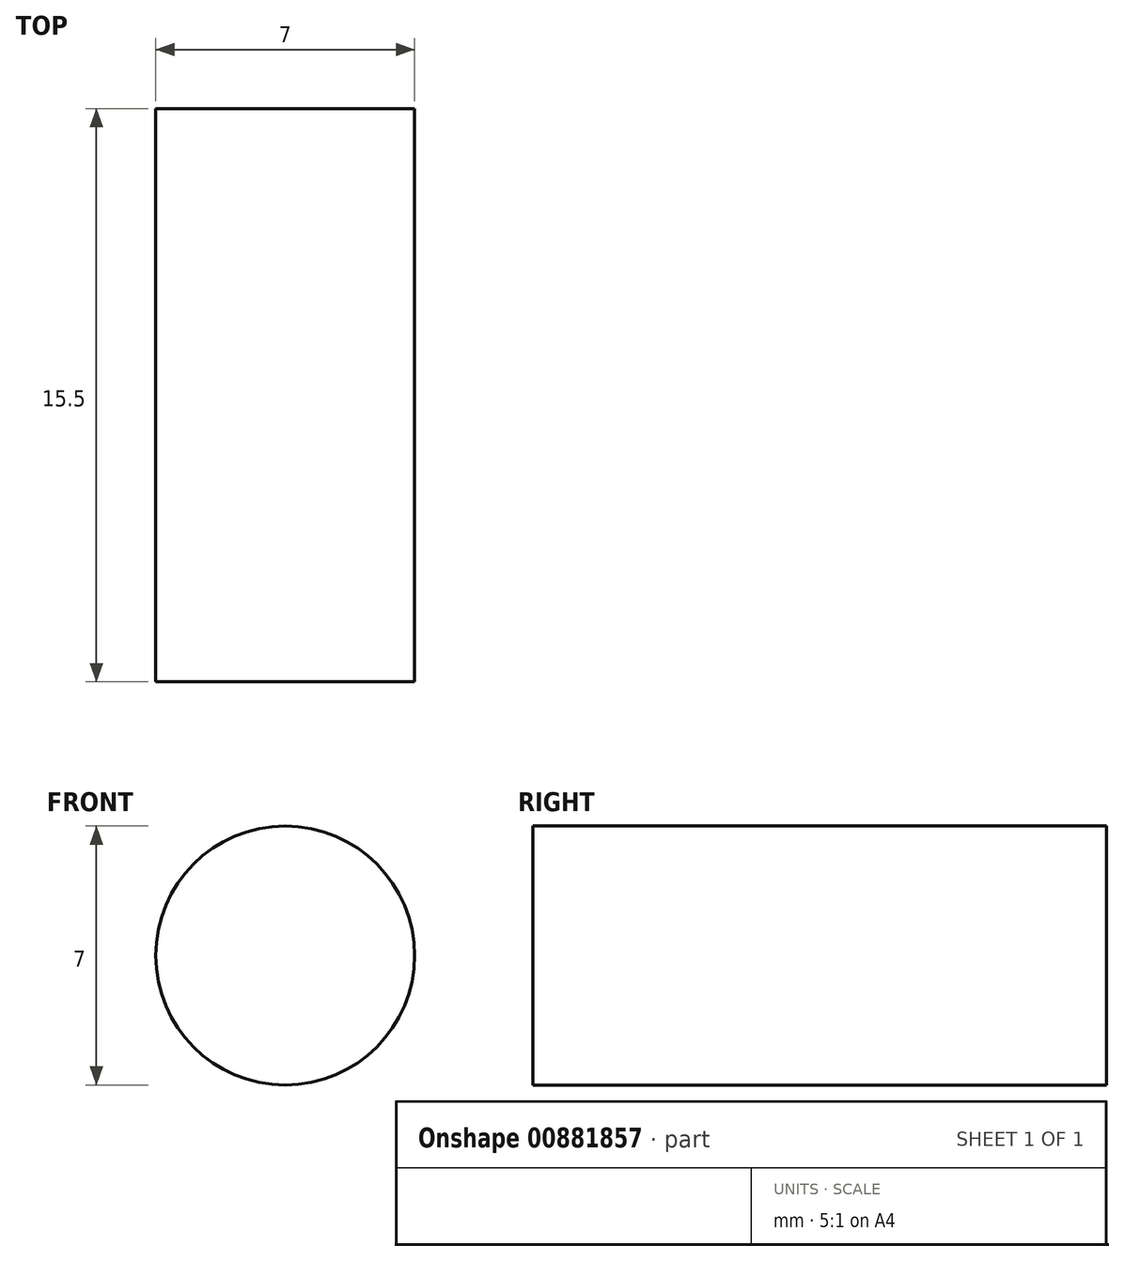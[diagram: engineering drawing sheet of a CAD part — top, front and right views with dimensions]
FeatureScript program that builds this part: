
annotation { "Feature Type Name" : "Feature", "Feature Type Description" : "" }
export const myFeature = defineFeature(function(context is Context, id is Id, definition is map)
    precondition{}
    {
        {
            var Q0;
            Q0=qCreatedBy(makeId("Top.planeOp"),FACE);
            var sketch = newSketch(context, id + "F0", { "sketchPlane" : qUnion([Q0])});
            skLineSegment(sketch, "E0.bottom", {"start": v(0, 0) * mm, "end": v(34, 0) * mm});
            skLineSegment(sketch, "E0.top", {"start": v(0, 15.5) * mm, "end": v(34, 15.5) * mm});
            skLineSegment(sketch, "E0.left", {"start": v(0, 0) * mm, "end": v(0, 15.5) * mm});
            skLineSegment(sketch, "E0.right", {"start": v(34, 0) * mm, "end": v(34, 15.5) * mm});
            skSolve(sketch);
        }
        {
            var Q0;
            Q0 = qSketchRegion(id + "F0", true);
            extrude(context, id + "F1", {"entities" : qUnion([Q0]), "depth" : 234 * mm, "offsetDistance" : 25 * mm});
        }
        {
            var Q0;
            Q0=makeQuery(id+"F1.opExtrude","SWEPT_FACE",FACE,{"disambiguationData":[OSD([sQuery(id+"F0.wireOp",EDGE,"E0.top")])]});
            var sketch = newSketch(context, id + "F2", { "sketchPlane" : qUnion([Q0])});
            skLineSegment(sketch, "E1", {"start": v(-34, 117) * mm, "end": v(0, 117) * mm, "construction": true});
            skCircle(sketch, "E2", {"center": v(-17, 67) * mm, "radius": 3.5 * mm});
            skCircle(sketch, "E3.MirrorC", {"center": v(-17, 167) * mm, "radius": 3.5 * mm});
            skSolve(sketch);
        }
        {
            var Q0;
            Q0=makeQuery(id+"F2.imprint","IMPRINT",FACE,{"disambiguationData":[TD([[makeQuery(id+"F2.imprint","IMPRINT",EDGE,{"derivedFrom":sQuery(id+"F2.wireOp",EDGE,"E3.MirrorC")}),-1.0]])]});
            var Q1;
            Q1=makeQuery(id+"F2.imprint","IMPRINT",FACE,{"disambiguationData":[TD([[makeQuery(id+"F2.imprint","IMPRINT",EDGE,{"derivedFrom":sQuery(id+"F2.wireOp",EDGE,"E2")}),1.0]])]});
            extrude(context, id + "F3", {"entities" : qUnion([Q0, Q1]), "operationType" : NewBodyOperationType.REMOVE, "oppositeDirection" : true, "depth" : 25 * mm, "offsetDistance" : 25 * mm});
        }
    });
